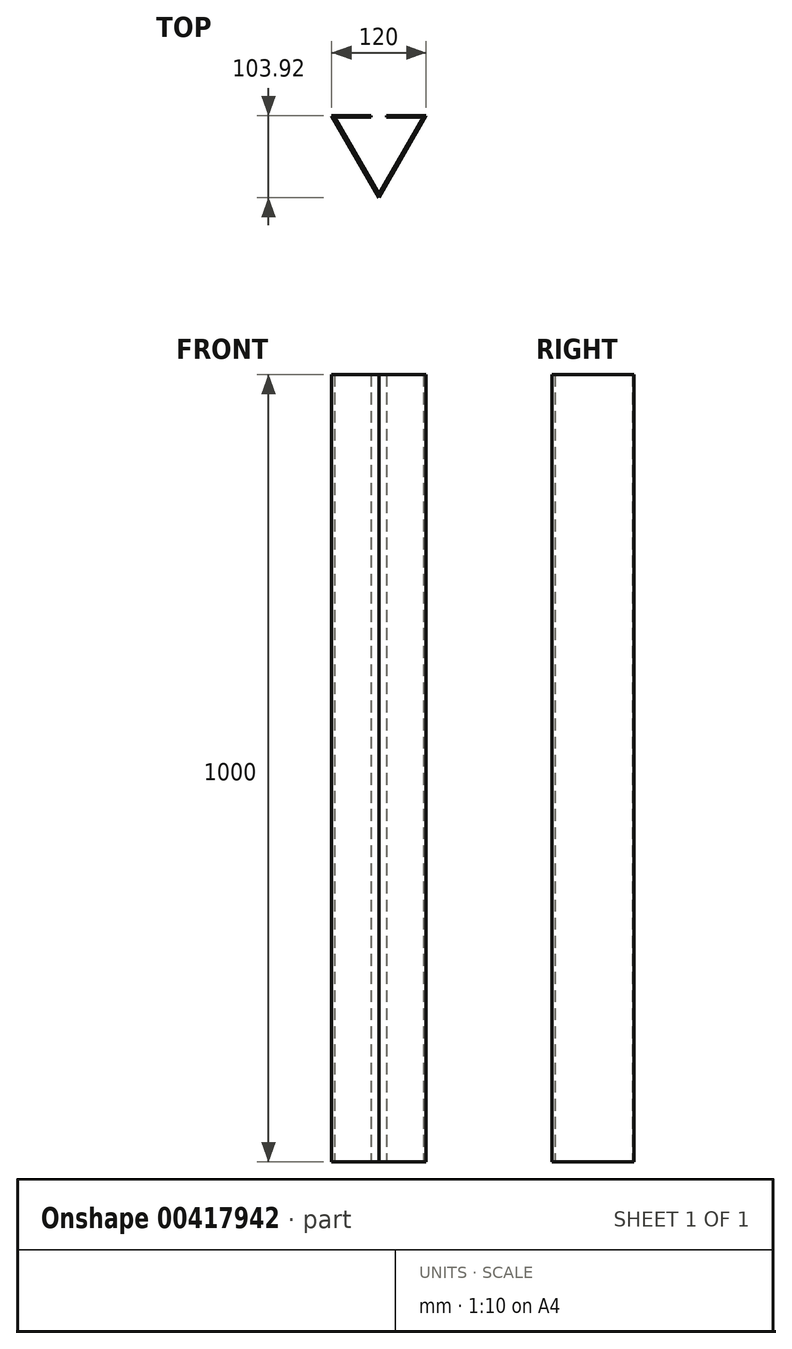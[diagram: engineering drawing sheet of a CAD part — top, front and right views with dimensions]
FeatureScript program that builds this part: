
annotation { "Feature Type Name" : "Feature", "Feature Type Description" : "" }
export const myFeature = defineFeature(function(context is Context, id is Id, definition is map)
    precondition{}
    {
        {
            var Q0;
            Q0=qCreatedBy(makeId("Top.planeOp"),FACE);
            var sketch = newSketch(context, id + "F0", { "sketchPlane" : qUnion([Q0])});
            skCircle(sketch, "E0.cCircle", {"center": v(0, 0) * mm, "radius": 69.28 * mm, "construction": true});
            skLineSegment(sketch, "E0.0", {"start": v(0, -69.28) * mm, "end": v(-60, 34.64) * mm});
            skLineSegment(sketch, "E0.1", {"start": v(-60, 34.64) * mm, "end": v(-9.9, 34.64) * mm});
            skLineSegment(sketch, "E0.2", {"start": v(60, 34.64) * mm, "end": v(0, -69.28) * mm});
            skLineSegment(sketch, "E1", {"start": v(10, 34.64) * mm, "end": v(60, 34.64) * mm});
            skLineSegment(sketch, "E2.0", {"start": v(-56.54, 32.64) * mm, "end": v(-9.9, 32.64) * mm});
            skLineSegment(sketch, "E2.1", {"start": v(0, -65.28) * mm, "end": v(-56.54, 32.64) * mm});
            skLineSegment(sketch, "E2.2", {"start": v(56.54, 32.64) * mm, "end": v(0, -65.28) * mm});
            skLineSegment(sketch, "E2.3", {"start": v(10, 32.64) * mm, "end": v(56.54, 32.64) * mm});
            skLineSegment(sketch, "E3", {"start": v(-9.9, 34.64) * mm, "end": v(-9.9, 32.64) * mm});
            skLineSegment(sketch, "E4", {"start": v(10, 34.64) * mm, "end": v(10, 32.64) * mm});
            skSolve(sketch);
        }
        {
            var Q0;
            Q0=makeQuery(id+"F0.imprint","IMPRINT",FACE,{"disambiguationData":[TD([[makeQuery(id+"F0.imprint","IMPRINT",EDGE,{"derivedFrom":sQuery(id+"F0.wireOp",EDGE,"E0.0")}),-1.0]])]});
            extrude(context, id + "F1", {"entities" : qUnion([Q0]), "depth" : 1000 * mm, "offsetDistance" : 25 * mm});
        }
    });
